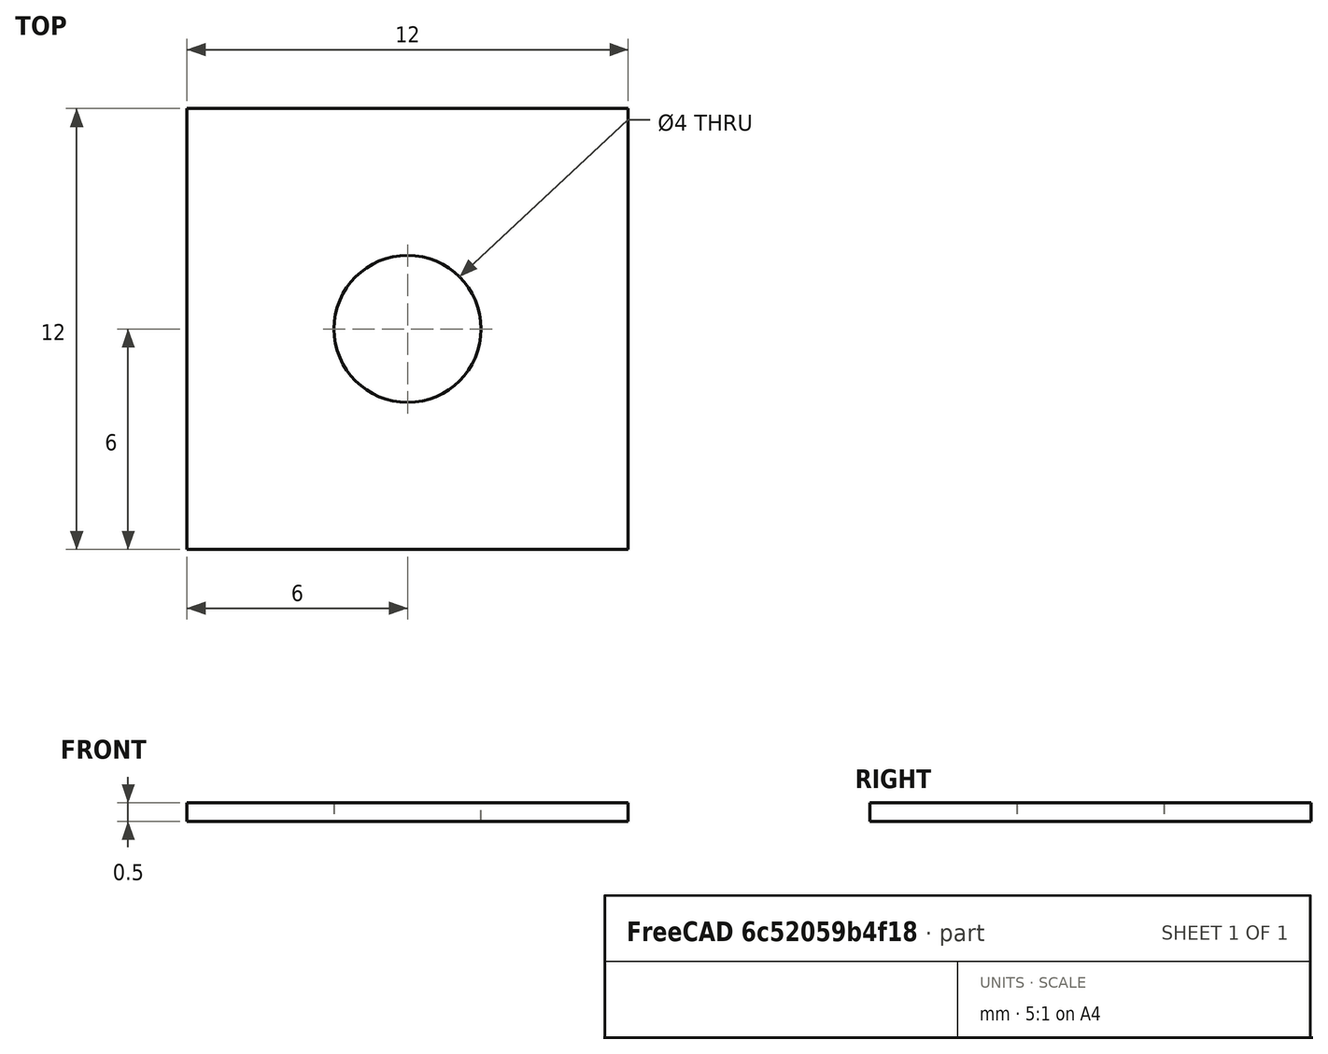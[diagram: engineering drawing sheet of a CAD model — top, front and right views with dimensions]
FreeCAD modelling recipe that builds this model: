
FCSTD DOCUMENT  (FreeCAD 1.0R39109 (Git))
Label: button
License: All rights reserved
LicenseURL: https://en.wikipedia.org/wiki/All_rights_reserved
objects: Sketcher::SketchObject×1, PartDesign::Pad×1, PartDesign::Body×1
note: 6 computed .brp shape members not serialized (recipe doc carries the construction recipe); baked Part::Feature solids carry a one-line shape summary decoded from their .brp

FEATURE [Sketcher::SketchObject] Sketch
  ArcFitTolerance = 1e-06
  AttachmentSupport = -> [XY_Plane]
  FullyConstrained = true
  MakeInternals = false
  MapMode = 5
  sketch-geometry (5):
    g0: LineSegment StartX=-6 StartY=6 StartZ=0 EndX=-6 EndY=-6 EndZ=0
    g1: LineSegment StartX=-6 StartY=-6 StartZ=0 EndX=6 EndY=-6 EndZ=0
    g2: LineSegment StartX=6 StartY=-6 StartZ=0 EndX=6 EndY=6 EndZ=0
    g3: LineSegment StartX=6 StartY=6 StartZ=0 EndX=-6 EndY=6 EndZ=0
    g4: Circle CenterX=0 CenterY=0 CenterZ=0 NormalX=0 NormalY=0 NormalZ=1 AngleXU=0 Radius=2
  constraints (12):
    c: Coincident(g0,g1)
    c: Coincident(g1,g2)
    c: Coincident(g2,g3)
    c: Coincident(g3,g0)
    c: Vertical(g2)
    c: Horizontal(g1)
    c: Symmetric(g0,g2,g-2)
    c: Symmetric(g0,g0,g-1)
    c: DistanceX(g3,g3) = 12
    c: DistanceY(g0,g0) = 12
    c: Diameter(g4) = 4
    c: Coincident(g4,g-1)
FEATURE [PartDesign::Pad] Pad
  Direction = (0,0,1)
  Length = 0.5
  Length2 = 10
  Profile = -> Sketch
  ReferenceAxis = -> Sketch [N_Axis]
  Refine = true
  Suppressed = false
  Type = 0
FEATURE [PartDesign::Body] Body
  AllowCompound = false
  Group = -> [Sketch,Pad]
  Origin = -> Origin
  Tip = -> Pad
